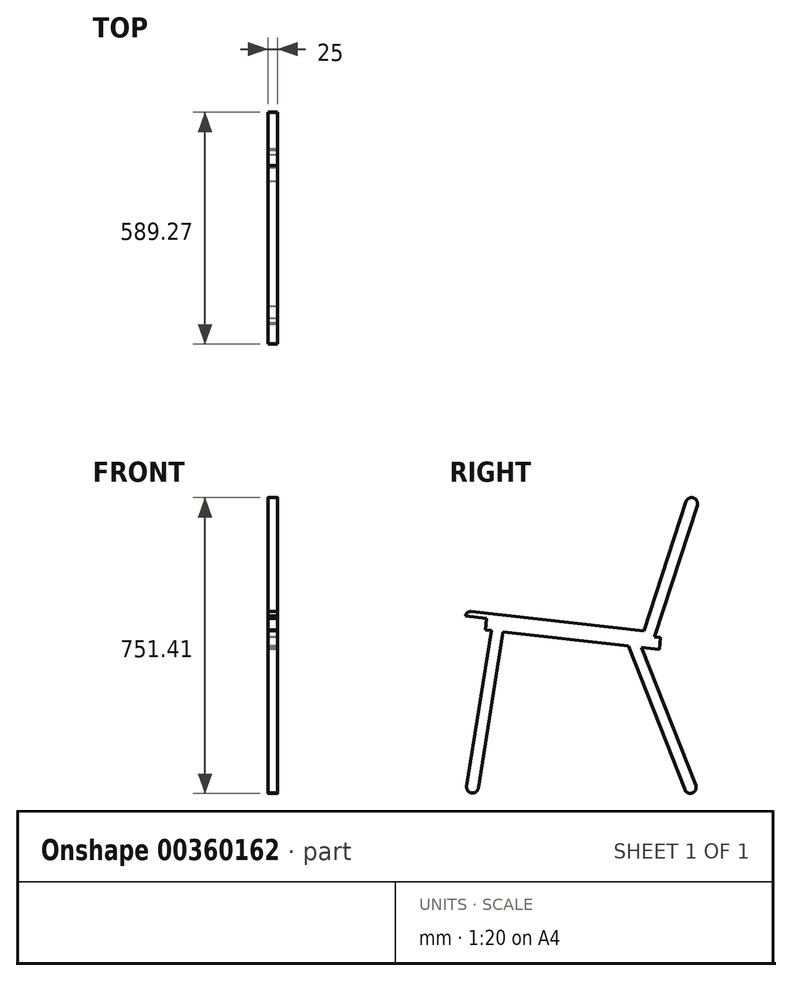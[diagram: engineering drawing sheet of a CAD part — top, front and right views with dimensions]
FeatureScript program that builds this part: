
annotation { "Feature Type Name" : "Feature", "Feature Type Description" : "" }
export const myFeature = defineFeature(function(context is Context, id is Id, definition is map)
    precondition{}
    {
        {
            var Q0;
            Q0=qCreatedBy(makeId("Right.planeOp"),FACE);
            var sketch = newSketch(context, id + "F0", { "sketchPlane" : qUnion([Q0])});
            skLineSegment(sketch, "E0", {"start": v(0, 0) * mm, "end": v(-110, 0) * mm, "construction": true});
            skLineSegment(sketch, "E1", {"start": v(-110, 0) * mm, "end": v(-510, 0) * mm, "construction": true});
            skLineSegment(sketch, "E2", {"start": v(-510, 0) * mm, "end": v(-560, 0) * mm, "construction": true});
            skLineSegment(sketch, "E3", {"start": v(-560, 0) * mm, "end": v(-560, 450) * mm, "construction": true});
            skLineSegment(sketch, "E4", {"start": v(-110, 0) * mm, "end": v(-110, 400) * mm, "construction": true});
            skLineSegment(sketch, "E5", {"start": v(-560, 450) * mm, "end": v(-110, 400) * mm, "construction": true});
            skLineSegment(sketch, "E6", {"start": v(0, 0) * mm, "end": v(0, 740) * mm, "construction": true});
            skLineSegment(sketch, "E7", {"start": v(-110, 400) * mm, "end": v(-78.47, 400) * mm, "construction": true});
            skLineSegment(sketch, "E8", {"start": v(0, 740) * mm, "end": v(-110, 400) * mm});
            skLineSegment(sketch, "E9.0", {"start": v(28.54, 730.77) * mm, "end": v(-78.47, 400) * mm});
            skPoint(sketch, "E10", {"position": v(25.27, 21.25) * mm});
            skArc(sketch, "E11", {"start": v(28.54, 730.77) * mm, "mid": v(18.89, 749.65) * mm, "end": v(0, 740) * mm});
            skPoint(sketch, "E12", {"position": v(-510, 444.44) * mm});
            skLineSegment(sketch, "E13", {"start": v(-121.93, 401.33) * mm, "end": v(-510, 444.44) * mm});
            skLineSegment(sketch, "E14.0", {"start": v(-113.31, 370.18) * mm, "end": v(-464.85, 409.24) * mm});
            skLineSegment(sketch, "E15", {"start": v(-113.31, 370.18) * mm, "end": v(-112.86, 370.13) * mm});
            skLineSegment(sketch, "E16", {"start": v(-110, 400) * mm, "end": v(-110, 517.54) * mm, "construction": true});
            skLineSegment(sketch, "E17", {"start": v(-510, 444.44) * mm, "end": v(-560, 450) * mm});
            skLineSegment(sketch, "E18", {"start": v(-546.75, 460.6) * mm, "end": v(-113.12, 412.42) * mm});
            skLineSegment(sketch, "E19", {"start": v(-121.93, 401.33) * mm, "end": v(-119.48, 401.05) * mm});
            skLineSegment(sketch, "E20", {"start": v(-113.12, 412.42) * mm, "end": v(-106.23, 411.65) * mm});
            skLineSegment(sketch, "E21", {"start": v(-106.23, 411.65) * mm, "end": v(-118.16, 412.98) * mm});
            skArc(sketch, "E22", {"start": v(-106.23, 411.65) * mm, "mid": v(-110.66, 403.6) * mm, "end": v(-119.48, 401.05) * mm});
            skLineSegment(sketch, "E23", {"start": v(-119.48, 401.05) * mm, "end": v(-110, 400) * mm});
            skArc(sketch, "E24", {"start": v(-560, 450) * mm, "mid": v(-555.57, 458.05) * mm, "end": v(-546.75, 460.6) * mm});
            skLineSegment(sketch, "E25", {"start": v(-510, 0) * mm, "end": v(-490, 0) * mm, "construction": true});
            skLineSegment(sketch, "E26", {"start": v(-490, 0) * mm, "end": v(-490, 442.22) * mm, "construction": true});
            skLineSegment(sketch, "E27", {"start": v(-494.7, 412.56) * mm, "end": v(-557.28, 17.16) * mm});
            skLineSegment(sketch, "E28.0", {"start": v(-464.85, 409.24) * mm, "end": v(-527.65, 12.47) * mm});
            skArc(sketch, "E29", {"start": v(-557.28, 17.16) * mm, "mid": v(-544.81, 0) * mm, "end": v(-527.65, 12.47) * mm});
            skLineSegment(sketch, "E30", {"start": v(28.54, 730.77) * mm, "end": v(25.27, 0) * mm, "construction": true});
            skLineSegment(sketch, "E31", {"start": v(-3.33, 8.5) * mm, "end": v(-146.55, 373.88) * mm});
            skLineSegment(sketch, "E32.0", {"start": v(24.6, 19.44) * mm, "end": v(-112.86, 370.13) * mm});
            skLineSegment(sketch, "E33", {"start": v(0, 0) * mm, "end": v(42.7, 0) * mm, "construction": true});
            skArc(sketch, "E34", {"start": v(-3.33, 8.5) * mm, "mid": v(16.11, 0) * mm, "end": v(24.6, 19.44) * mm});
            skPoint(sketch, "E35.end.orphan", {"position": v(16.11, 0) * mm});
            skPoint(sketch, "E36", {"position": v(-78.47, 400) * mm});
            skLineSegment(sketch, "E37", {"start": v(-464.85, 409.24) * mm, "end": v(-494.7, 412.56) * mm});
            skLineSegment(sketch, "E38", {"start": v(-494.7, 412.56) * mm, "end": v(-509.6, 414.22) * mm});
            skLineSegment(sketch, "E39", {"start": v(-509.6, 414.22) * mm, "end": v(-506.3, 444.03) * mm});
            skLineSegment(sketch, "E40", {"start": v(-110, 400) * mm, "end": v(-79.56, 396.62) * mm});
            skLineSegment(sketch, "E41", {"start": v(-79.56, 396.62) * mm, "end": v(-64.65, 394.96) * mm});
            skLineSegment(sketch, "E42", {"start": v(-64.65, 394.96) * mm, "end": v(-67.97, 365.15) * mm});
            skLineSegment(sketch, "E43", {"start": v(-67.97, 365.15) * mm, "end": v(-117.7, 370.67) * mm});
            skLineSegment(sketch, "E44.trimOffspring", {"start": v(-63.47, 400) * mm, "end": v(0, 400) * mm, "construction": true});
            skLineSegment(sketch, "E45", {"start": v(-78.47, 400) * mm, "end": v(-79.56, 396.62) * mm});
            skPoint(sketch, "E46", {"position": v(-544.81, 0) * mm});
            skLineSegment(sketch, "E47", {"start": v(-161.09, 405.68) * mm, "end": v(-164.4, 375.86) * mm});
            skLineSegment(sketch, "E48", {"start": v(-146.55, 373.88) * mm, "end": v(-159.01, 405.68) * mm, "construction": true});
            skSolve(sketch);
        }
        {
            var Q0;
            {var subQ0=sQuery(id+"F0.wireOp",EDGE,"E31");Q0=makeQuery(id+"F0.imprint","IMPRINT",FACE,{"disambiguationData":[TD([[makeQuery(id+"F0.imprint","IMPRINT",EDGE,{"derivedFrom":subQ0}),-1.0]])]});}
            var Q1;
            Q1=makeQuery(id+"F0.imprint","IMPRINT",FACE,{"disambiguationData":[TD([[makeQuery(id+"F0.imprint","IMPRINT",EDGE,{"derivedFrom":sQuery(id+"F0.wireOp",EDGE,"E27")}),1.0]])]});
            var Q2;
            Q2=makeQuery(id+"F0.imprint","IMPRINT",FACE,{"disambiguationData":[TD([[makeQuery(id+"F0.imprint","IMPRINT",EDGE,{"derivedFrom":sQuery(id+"F0.wireOp",EDGE,"E9.0")}),-1.0]])]});
            var Q3;
            {var subQ0=sQuery(id+"F0.wireOp",EDGE,"E37");Q3=makeQuery(id+"F0.imprint","IMPRINT",FACE,{"disambiguationData":[TD([[makeQuery(id+"F0.imprint","IMPRINT",EDGE,{"derivedFrom":subQ0}),-1.0]])]});}
            var Q4;
            {var subQ0=sQuery(id+"F0.wireOp",EDGE,"E17");Q4=makeQuery(id+"F0.imprint","IMPRINT",FACE,{"disambiguationData":[TD([[makeQuery(id+"F0.imprint","IMPRINT",EDGE,{"derivedFrom":subQ0}),-1.0]])]});}
            var Q5;
            {var subQ6=sQuery(id+"F0.wireOp",EDGE,"E19");Q5=makeQuery(id+"F0.imprint","IMPRINT",FACE,{"disambiguationData":[TD([[makeQuery(id+"F0.imprint","IMPRINT",EDGE,{"derivedFrom":subQ6}),-1.0]])]});}
            var Q6;
            {var subQ0=sQuery(id+"F0.wireOp",EDGE,"E22");var subQ1=sQuery(id+"F0.wireOp",EDGE,"E8");var subQ3=makeQuery(id+"F0.imprint","INTERSECT",VERTEX,{"derivedFrom":[subQ1,subQ0]});Q6=makeQuery(id+"F0.imprint","IMPRINT",FACE,{"disambiguationData":[TD([[makeQuery(id+"F0.imprint","IMPRINT",EDGE,{"disambiguationData":[TD([[subQ3,1.0]])],"derivedFrom":subQ1}),1.0]])]});}
            var Q7;
            {var subQ0=sQuery(id+"F0.wireOp",EDGE,"E23");Q7=makeQuery(id+"F0.imprint","IMPRINT",FACE,{"disambiguationData":[TD([[makeQuery(id+"F0.imprint","IMPRINT",EDGE,{"derivedFrom":subQ0}),1.0]])]});}
            extrude(context, id + "F1", {"entities" : qUnion([Q0, Q1, Q2, Q3, Q4, Q5, Q6, Q7]), "depth" : 25 * mm});
        }
    });
